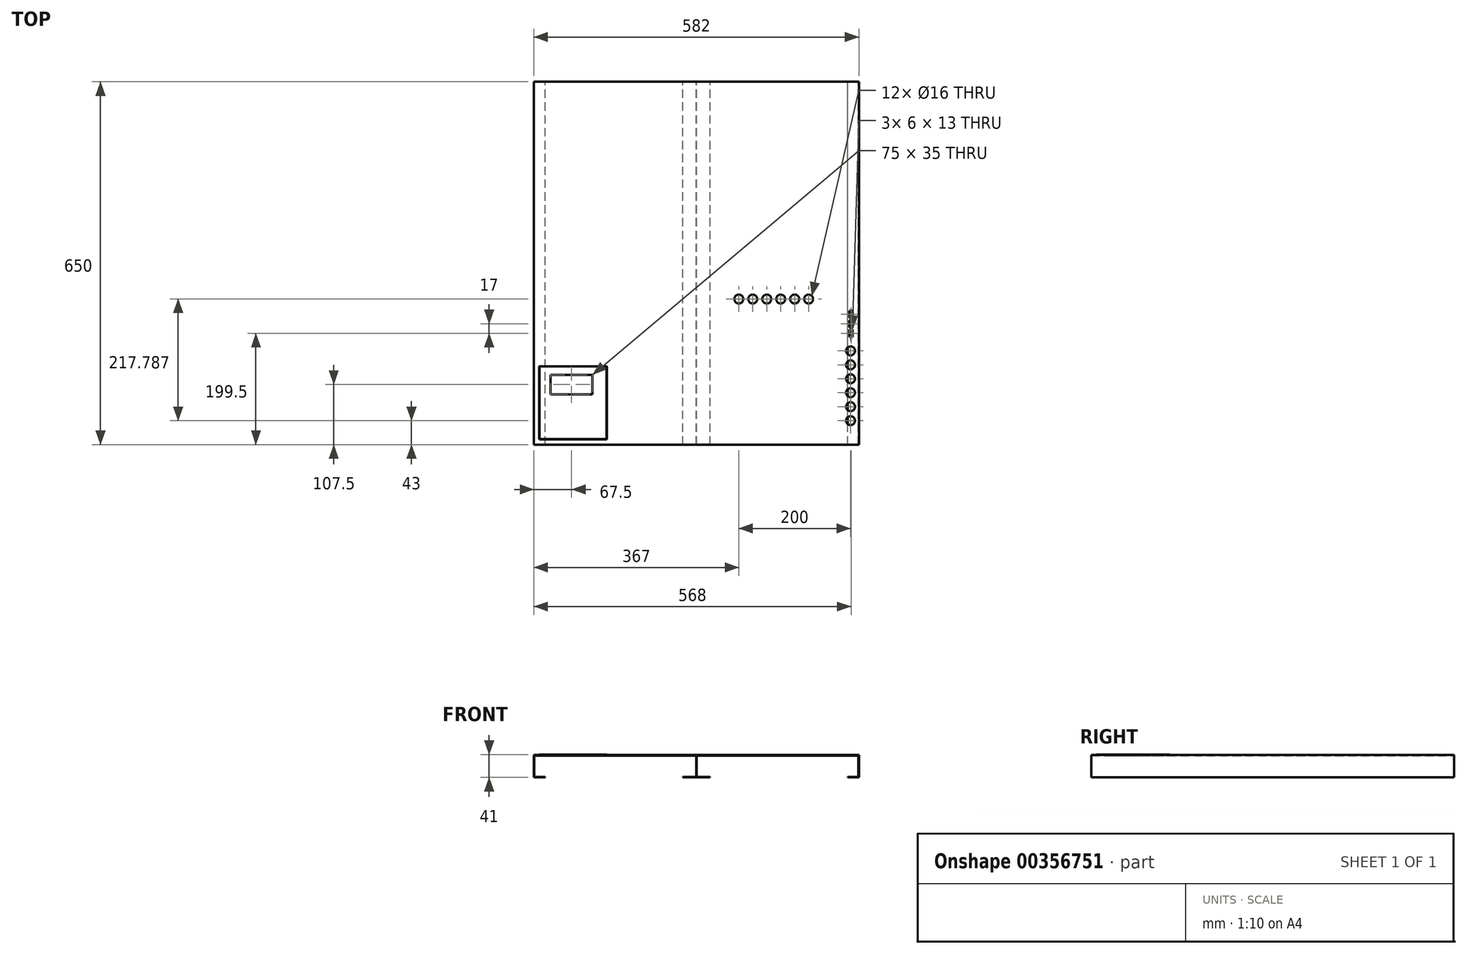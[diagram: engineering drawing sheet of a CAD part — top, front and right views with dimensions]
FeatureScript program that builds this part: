
annotation { "Feature Type Name" : "Feature", "Feature Type Description" : "" }
export const myFeature = defineFeature(function(context is Context, id is Id, definition is map)
    precondition{}
    {
        {
            var Q0;
            Q0=qCreatedBy(makeId("Front.planeOp"),FACE);
            var sketch = newSketch(context, id + "F0", { "sketchPlane" : qUnion([Q0])});
            skLineSegment(sketch, "E0.bottom", {"start": v(-291, -20) * mm, "end": v(-271, -20) * mm});
            skLineSegment(sketch, "E0.top", {"start": v(-291, 20) * mm, "end": v(291, 20) * mm});
            skLineSegment(sketch, "E0.left", {"start": v(-291, -20) * mm, "end": v(-291, 20) * mm});
            skLineSegment(sketch, "E0.right", {"start": v(291, -20) * mm, "end": v(291, 20) * mm});
            skPoint(sketch, "E0.middle", {"position": v(0, 0) * mm});
            skPoint(sketch, "E1", {"position": v(-271, -20) * mm});
            skPoint(sketch, "E2", {"position": v(271, -20) * mm});
            skLineSegment(sketch, "E3.trimOffspring", {"start": v(271, -20) * mm, "end": v(291, -20) * mm});
            skLineSegment(sketch, "E4.0", {"start": v(271, -19.1) * mm, "end": v(290.1, -19.1) * mm});
            skLineSegment(sketch, "E4.1", {"start": v(-290.1, -19.1) * mm, "end": v(-271, -19.1) * mm});
            skLineSegment(sketch, "E4.2", {"start": v(-290.1, -19.1) * mm, "end": v(-290.1, 19.1) * mm});
            skLineSegment(sketch, "E4.3", {"start": v(-290.1, 19.1) * mm, "end": v(290.1, 19.1) * mm});
            skLineSegment(sketch, "E4.4", {"start": v(290.1, -19.1) * mm, "end": v(290.1, 19.1) * mm});
            skLineSegment(sketch, "E5", {"start": v(-271, -19.1) * mm, "end": v(-271, -20) * mm});
            skLineSegment(sketch, "E6", {"start": v(271, -19.1) * mm, "end": v(271, -20) * mm});
            skSolve(sketch);
        }
        {
            var Q0;
            Q0=makeQuery(id+"F0.imprint","IMPRINT",FACE,{"disambiguationData":[TD([[makeQuery(id+"F0.imprint","IMPRINT",EDGE,{"derivedFrom":sQuery(id+"F0.wireOp",EDGE,"E0.bottom")}),1.0]])]});
            extrude(context, id + "F1", {"entities" : qUnion([Q0]), "endBound" : BoundingType.SYMMETRIC, "depth" : 650 * mm});
        }
        {
            var Q0;
            Q0=makeQuery(id+"F1.opExtrude","SWEPT_FACE",FACE,{"disambiguationData":[OSD([sQuery(id+"F0.wireOp",EDGE,"E0.top")])]});
            var sketch = newSketch(context, id + "F2", { "sketchPlane" : qUnion([Q0])});
            skLineSegment(sketch, "E7.bottom", {"start": v(-161, -185) * mm, "end": v(-281, -185) * mm, "construction": true});
            skLineSegment(sketch, "E7.top", {"start": v(-161, -315) * mm, "end": v(-281, -315) * mm, "construction": true});
            skLineSegment(sketch, "E7.left", {"start": v(-161, -185) * mm, "end": v(-161, -315) * mm, "construction": true});
            skLineSegment(sketch, "E7.right", {"start": v(-281, -185) * mm, "end": v(-281, -315) * mm, "construction": true});
            skPoint(sketch, "E7.middle", {"position": v(-221, -250) * mm});
            skLineSegment(sketch, "E8.bottom", {"start": v(251, -85) * mm, "end": v(-159, -85) * mm, "construction": true});
            skLineSegment(sketch, "E8.top", {"start": v(251, -315) * mm, "end": v(-159, -315) * mm, "construction": true});
            skLineSegment(sketch, "E8.left", {"start": v(251, -85) * mm, "end": v(251, -315) * mm, "construction": true});
            skLineSegment(sketch, "E8.right", {"start": v(-159, -85) * mm, "end": v(-159, -315) * mm, "construction": true});
            skPoint(sketch, "E8.middle", {"position": v(46, -200) * mm});
            skCircle(sketch, "E9", {"center": v(276, -207) * mm, "radius": 8 * mm});
            skCircle(sketch, "E10", {"center": v(276, -282) * mm, "radius": 8 * mm});
            skCircle(sketch, "E11", {"center": v(276, -232) * mm, "radius": 8 * mm});
            skCircle(sketch, "E12", {"center": v(276, -257) * mm, "radius": 8 * mm});
            skCircle(sketch, "E13", {"center": v(276, -182) * mm, "radius": 8 * mm});
            skLineSegment(sketch, "E14.bottom", {"start": v(-261, -235) * mm, "end": v(-186, -235) * mm});
            skLineSegment(sketch, "E14.top", {"start": v(-261, -200) * mm, "end": v(-186, -200) * mm});
            skLineSegment(sketch, "E14.left", {"start": v(-261, -235) * mm, "end": v(-261, -200) * mm});
            skLineSegment(sketch, "E14.right", {"start": v(-186, -235) * mm, "end": v(-186, -200) * mm});
            skLineSegment(sketch, "E15.bottom", {"start": v(280, -119) * mm, "end": v(274, -119) * mm});
            skLineSegment(sketch, "E15.top", {"start": v(280, -132) * mm, "end": v(274, -132) * mm});
            skLineSegment(sketch, "E15.left", {"start": v(280, -119) * mm, "end": v(280, -132) * mm});
            skLineSegment(sketch, "E15.right", {"start": v(274, -119) * mm, "end": v(274, -132) * mm});
            skCircle(sketch, "E16", {"center": v(201, -64.21) * mm, "radius": 8 * mm});
            skCircle(sketch, "E17", {"center": v(176, -64.21) * mm, "radius": 8 * mm});
            skCircle(sketch, "E18", {"center": v(151, -64.21) * mm, "radius": 8 * mm});
            skCircle(sketch, "E19", {"center": v(126, -64.21) * mm, "radius": 8 * mm});
            skCircle(sketch, "E20", {"center": v(101, -64.21) * mm, "radius": 8 * mm});
            skCircle(sketch, "E21", {"center": v(76, -64.21) * mm, "radius": 8 * mm});
            skCircle(sketch, "E22", {"center": v(276, -157) * mm, "radius": 8 * mm});
            skLineSegment(sketch, "E23.bottom", {"start": v(280, -102) * mm, "end": v(274, -102) * mm});
            skLineSegment(sketch, "E23.top", {"start": v(280, -115) * mm, "end": v(274, -115) * mm});
            skLineSegment(sketch, "E23.left", {"start": v(280, -102) * mm, "end": v(280, -115) * mm});
            skLineSegment(sketch, "E23.right", {"start": v(274, -102) * mm, "end": v(274, -115) * mm});
            skLineSegment(sketch, "E24.bottom", {"start": v(280, -85) * mm, "end": v(274, -85) * mm});
            skLineSegment(sketch, "E24.top", {"start": v(280, -98) * mm, "end": v(274, -98) * mm});
            skLineSegment(sketch, "E24.left", {"start": v(280, -85) * mm, "end": v(280, -98) * mm});
            skLineSegment(sketch, "E24.right", {"start": v(274, -85) * mm, "end": v(274, -98) * mm});
            skSolve(sketch);
        }
        {
            var Q0;
            Q0=sQuery(id+"F2.wireOp",VERTEX,"E10.center");
            var Q1;
            Q1=sQuery(id+"F2.wireOp",VERTEX,"E12.center");
            var Q2;
            Q2=sQuery(id+"F2.wireOp",VERTEX,"E11.center");
            var Q3;
            Q3=sQuery(id+"F2.wireOp",VERTEX,"E9.center");
            var Q4;
            Q4=sQuery(id+"F2.wireOp",VERTEX,"E13.center");
            var Q5;
            Q5=sQuery(id+"F2.wireOp",VERTEX,"ZPgRsYmq-daMn-rLE5-gk4w-gas4kPWKtT1p.center");
            var Q6;
            Q6=sQuery(id+"F2.wireOp",VERTEX,"E16.center");
            var Q7;
            Q7=sQuery(id+"F2.wireOp",VERTEX,"E17.center");
            var Q8;
            Q8=sQuery(id+"F2.wireOp",VERTEX,"E18.center");
            var Q9;
            Q9=sQuery(id+"F2.wireOp",VERTEX,"E19.center");
            var Q10;
            Q10=sQuery(id+"F2.wireOp",VERTEX,"E20.center");
            var Q11;
            Q11=sQuery(id+"F2.wireOp",VERTEX,"E21.center");
            var Q12;
            Q12=sQuery(id+"F2.wireOp",VERTEX,"E22.center");
            var Q13;
            Q13=makeQuery(id+"F1.opExtrude","SWEPT_BODY",BODY,{"disambiguationData":[OSD([sQuery(id+"F0.wireOp",EDGE,"E0.bottom"),sQuery(id+"F0.wireOp",EDGE,"E0.top"),sQuery(id+"F0.wireOp",EDGE,"E0.left"),sQuery(id+"F0.wireOp",EDGE,"E0.right"),sQuery(id+"F0.wireOp",EDGE,"E3.trimOffspring"),sQuery(id+"F0.wireOp",EDGE,"E4.0"),sQuery(id+"F0.wireOp",EDGE,"E4.1"),sQuery(id+"F0.wireOp",EDGE,"E4.2"),sQuery(id+"F0.wireOp",EDGE,"E4.3"),sQuery(id+"F0.wireOp",EDGE,"E4.4"),sQuery(id+"F0.wireOp",EDGE,"E5"),sQuery(id+"F0.wireOp",EDGE,"E6")])]});
            hole(context, id + "F3", {"style" : HoleStyle.SIMPLE, "endStyle" : HoleEndStyle.BLIND, "holeDiameter" : 16 * mm, "holeDepth" : 5 * mm, "isTappedThrough" : true, "tappedDepth" : 12 * mm, "tapClearance" : 3, "startFromSketch" : true, "locations" : qUnion([Q0, Q1, Q2, Q3, Q4, Q5, Q6, Q7, Q8, Q9, Q10, Q11, Q12]), "scope" : qUnion([Q13])});
        }
        {
            var Q0;
            Q0=makeQuery(id+"F2.imprint","IMPRINT",FACE,{"disambiguationData":[TD([[makeQuery(id+"F2.imprint","IMPRINT",EDGE,{"derivedFrom":sQuery(id+"F2.wireOp",EDGE,"E15.bottom")}),1.0]])]});
            var Q1;
            Q1=makeQuery(id+"F2.imprint","IMPRINT",FACE,{"disambiguationData":[TD([[makeQuery(id+"F2.imprint","IMPRINT",EDGE,{"derivedFrom":sQuery(id+"F2.wireOp",EDGE,"E14.bottom")}),1.0]])]});
            var Q2;
            Q2=makeQuery(id+"F2.imprint","IMPRINT",FACE,{"disambiguationData":[TD([[makeQuery(id+"F2.imprint","IMPRINT",EDGE,{"derivedFrom":sQuery(id+"F2.wireOp",EDGE,"E23.bottom")}),1.0]])]});
            var Q3;
            Q3=makeQuery(id+"F2.imprint","IMPRINT",FACE,{"disambiguationData":[TD([[makeQuery(id+"F2.imprint","IMPRINT",EDGE,{"derivedFrom":sQuery(id+"F2.wireOp",EDGE,"E24.bottom")}),1.0]])]});
            extrude(context, id + "F4", {"entities" : qUnion([Q0, Q1, Q2, Q3]), "operationType" : NewBodyOperationType.REMOVE, "oppositeDirection" : true, "depth" : 25 * mm});
        }
        {
            var Q0;
            Q0=makeQuery(id+"F2.imprint","IMPRINT",FACE,{"disambiguationData":[TD([[makeQuery(id+"F2.imprint","IMPRINT",EDGE,{"derivedFrom":sQuery(id+"F2.wireOp",EDGE,"E9")}),-1.0]])]});
            var sketch = newSketch(context, id + "F5", { "sketchPlane" : qUnion([Q0])});
            skLineSegment(sketch, "E25.bottom", {"start": v(-280, -185) * mm, "end": v(-162, -185) * mm});
            skLineSegment(sketch, "E25.top", {"start": v(-280, -315) * mm, "end": v(-162, -315) * mm});
            skLineSegment(sketch, "E25.left", {"start": v(-281, -186) * mm, "end": v(-281, -314) * mm});
            skLineSegment(sketch, "E25.right", {"start": v(-161, -186) * mm, "end": v(-161, -314) * mm});
            skLineSegment(sketch, "E26.0", {"start": v(-280.5, -184.5) * mm, "end": v(-161.5, -184.5) * mm});
            skLineSegment(sketch, "E26.1", {"start": v(-281.5, -185.5) * mm, "end": v(-281.5, -314.5) * mm});
            skLineSegment(sketch, "E26.2", {"start": v(-280.5, -315.5) * mm, "end": v(-161.5, -315.5) * mm});
            skLineSegment(sketch, "E26.3", {"start": v(-160.5, -185.5) * mm, "end": v(-160.5, -314.5) * mm});
            skPoint(sketch, "E27.visualSharp", {"position": v(-161, -185) * mm});
            skArc(sketch, "E27.filletArc", {"start": v(-161, -186) * mm, "mid": v(-161.3, -185.3) * mm, "end": v(-162, -185) * mm});
            skPoint(sketch, "E28.visualSharp", {"position": v(-160.5, -184.5) * mm});
            skArc(sketch, "E28.filletArc", {"start": v(-160.5, -185.5) * mm, "mid": v(-160.8, -184.8) * mm, "end": v(-161.5, -184.5) * mm});
            skPoint(sketch, "E29.visualSharp", {"position": v(-281.5, -184.5) * mm});
            skArc(sketch, "E29.filletArc", {"start": v(-280.5, -184.5) * mm, "mid": v(-281.2, -184.8) * mm, "end": v(-281.5, -185.5) * mm});
            skPoint(sketch, "E30.visualSharp", {"position": v(-281, -185) * mm});
            skArc(sketch, "E30.filletArc", {"start": v(-280, -185) * mm, "mid": v(-280.7, -185.3) * mm, "end": v(-281, -186) * mm});
            skPoint(sketch, "E31.visualSharp", {"position": v(-281, -315) * mm});
            skArc(sketch, "E31.filletArc", {"start": v(-281, -314) * mm, "mid": v(-280.7, -314.7) * mm, "end": v(-280, -315) * mm});
            skPoint(sketch, "E32.visualSharp", {"position": v(-281.5, -315.5) * mm});
            skArc(sketch, "E32.filletArc", {"start": v(-281.5, -314.5) * mm, "mid": v(-281.2, -315.2) * mm, "end": v(-280.5, -315.5) * mm});
            skPoint(sketch, "E33.visualSharp", {"position": v(-160.5, -315.5) * mm});
            skArc(sketch, "E33.filletArc", {"start": v(-161.5, -315.5) * mm, "mid": v(-160.8, -315.2) * mm, "end": v(-160.5, -314.5) * mm});
            skPoint(sketch, "E34.visualSharp", {"position": v(-161, -315) * mm});
            skArc(sketch, "E34.filletArc", {"start": v(-162, -315) * mm, "mid": v(-161.3, -314.7) * mm, "end": v(-161, -314) * mm});
            skSolve(sketch);
        }
        {
            var Q0;
            Q0 = qSketchRegion(id + "F5", true);
            extrude(context, id + "F6", {"entities" : qUnion([Q0]), "operationType" : NewBodyOperationType.ADD, "depth" : 1 * mm});
        }
        {
            var Q0;
            Q0=qCreatedBy(makeId("Front.planeOp"),FACE);
            var sketch = newSketch(context, id + "F7", { "sketchPlane" : qUnion([Q0])});
            skLineSegment(sketch, "E35.bottom", {"start": v(24.36, -20) * mm, "end": v(-24.36, -20) * mm});
            skLineSegment(sketch, "E35.top", {"start": v(0.47, 20) * mm, "end": v(-0.43, 20) * mm});
            skLineSegment(sketch, "E35.left", {"start": v(24.36, -20) * mm, "end": v(24.36, -19.1) * mm});
            skLineSegment(sketch, "E35.right", {"start": v(-24.36, -20) * mm, "end": v(-24.36, -19.1) * mm});
            skPoint(sketch, "E35.middle", {"position": v(0, 0) * mm});
            skLineSegment(sketch, "E36", {"start": v(-0.43, 20) * mm, "end": v(-0.43, -19.1) * mm});
            skLineSegment(sketch, "E37", {"start": v(-0.43, -19.1) * mm, "end": v(-24.36, -19.1) * mm});
            skLineSegment(sketch, "E38", {"start": v(0.47, 20) * mm, "end": v(0.47, -19.1) * mm});
            skLineSegment(sketch, "E39", {"start": v(0.47, -19.1) * mm, "end": v(24.36, -19.1) * mm});
            skPoint(sketch, "E40.orphan", {"position": v(-24.36, 20) * mm});
            skPoint(sketch, "E41.orphan", {"position": v(24.36, 20) * mm});
            skSolve(sketch);
        }
        {
            var Q0;
            Q0 = qSketchRegion(id + "F7", true);
            extrude(context, id + "F8", {"entities" : qUnion([Q0]), "operationType" : NewBodyOperationType.ADD, "endBound" : BoundingType.SYMMETRIC, "depth" : 650 * mm});
        }
    });
